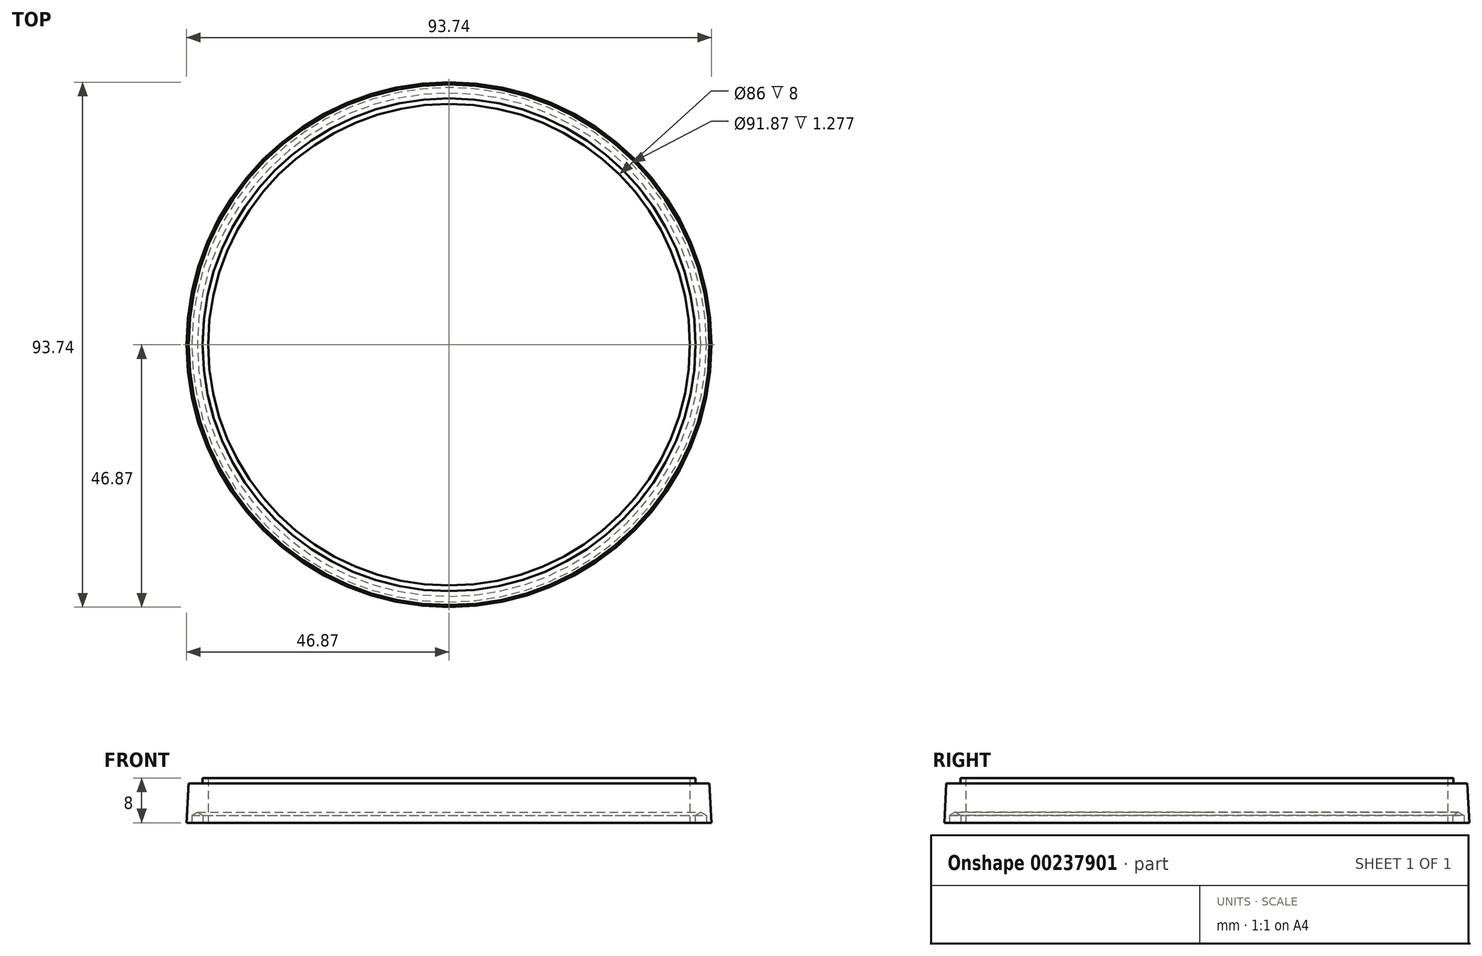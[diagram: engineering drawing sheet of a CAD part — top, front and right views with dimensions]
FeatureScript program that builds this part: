
annotation { "Feature Type Name" : "Feature", "Feature Type Description" : "" }
export const myFeature = defineFeature(function(context is Context, id is Id, definition is map)
    precondition{}
    {
        {
            var Q0;
            Q0=qCreatedBy(makeId("Front.planeOp"),FACE);
            var sketch = newSketch(context, id + "F0", { "sketchPlane" : qUnion([Q0])});
            skLineSegment(sketch, "E0", {"start": v(-46.87, 0) * mm, "end": v(-46.5, 7) * mm});
            skLineSegment(sketch, "E1", {"start": v(-46.5, 7) * mm, "end": v(-44, 7) * mm});
            skLineSegment(sketch, "E2", {"start": v(-44, 7) * mm, "end": v(-44, 8) * mm});
            skLineSegment(sketch, "E3", {"start": v(-44, 8) * mm, "end": v(-43, 8) * mm});
            skLineSegment(sketch, "E4", {"start": v(-46.87, 0) * mm, "end": v(-45.93, 0) * mm});
            skLineSegment(sketch, "E5", {"start": v(-43, 0) * mm, "end": v(-43, 8) * mm});
            skCircle(sketch, "E6.cCircle", {"center": v(-44.93, 0.7) * mm, "radius": 1 * mm, "construction": true});
            skPoint(sketch, "E6.cCircle.centerSnap0", {"position": v(-44.93, 0) * mm});
            skLineSegment(sketch, "E6.0", {"start": v(-45.93, 0.12) * mm, "end": v(-45.93, 1.28) * mm});
            skLineSegment(sketch, "E6.1", {"start": v(-45.93, 1.28) * mm, "end": v(-44.93, 1.85) * mm});
            skLineSegment(sketch, "E6.2", {"start": v(-44.93, 1.85) * mm, "end": v(-43.93, 1.28) * mm});
            skLineSegment(sketch, "E6.3", {"start": v(-43.93, 1.28) * mm, "end": v(-43.93, 0) * mm});
            skPoint(sketch, "E6.0.midPoint", {"position": v(-45.93, 0.7) * mm});
            skLineSegment(sketch, "E7.trimOffspring", {"start": v(-43.93, 0) * mm, "end": v(-43, 0) * mm});
            skLineSegment(sketch, "E8", {"start": v(-45.93, 0.12) * mm, "end": v(-45.93, 0) * mm});
            skLineSegment(sketch, "E9", {"start": v(0, 0) * mm, "end": v(0, 6.77) * mm, "construction": true});
            skSolve(sketch);
        }
        {
            var Q0;
            Q0=makeQuery(id+"F0.imprint","IMPRINT",FACE,{"disambiguationData":[TD([[makeQuery(id+"F0.imprint","IMPRINT",EDGE,{"derivedFrom":sQuery(id+"F0.wireOp",EDGE,"E0")}),-1.0]])]});
            var Q1;
            Q1=sQuery(id+"F0.wireOp",EDGE,"E9");
            revolve(context, id + "F1", {"surfaceOperationType" : NewSurfaceOperationType.NEW, "entities" : qUnion([Q0]), "axis" : qUnion([Q1]), "revolveType" : RevolveType.FULL});
        }
    });
